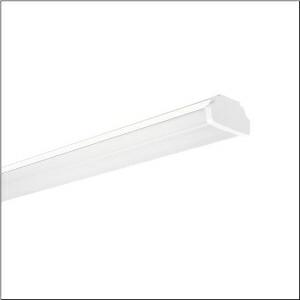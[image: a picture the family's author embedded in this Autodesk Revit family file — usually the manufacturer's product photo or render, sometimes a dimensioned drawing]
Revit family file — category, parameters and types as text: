
# Revit family: modario_r__31_gen_2_53bm8127v68xc2_4e77
name_source: partatom
category: Lighting Fixtures
units: mm (PartAtom-declared; Revit-internal decimal feet)

## family parameters
Cut with Voids When Loaded = No
Host = Face
Light Source = No
Part Type = Normal
Room Calculation Point = No
Round Connector Dimension = Use Diameter
Shared = No

## types (1)
- Modario® 31 Gen.2 (1 x LED, 8340 lm, 47.9 W, 6500K)
    Apparent Load = 48 VA
    CIE Flux Codes = 47 80 95 93 100
    Color Rendering = 80
    Color Temperature = 6500K
    Default Elevation = 1800 mm
    Description = Modario® 31 Gen.2, luminaire insert, of sheet steel, coil coated, white, length: 1.495mm, width: 81mm, height: 82mm, 5x system unit, system units: 299mm, LED rated luminous flux: 8.340lm, light colour: 865, control gear: ON/OFF, control gear: ECG, with plug, 3-pole, with phase selection, mains connection: 220..240V, AC, 50/60Hz, rated input power: 48W, through-wiring accessed according to module size, primary optical cover: cover, of PMMA, light emission: direct distribution, primary light characteristic: symmetric, protection rating (complete): IP20, protection rating (LED compartment): IP50, insulation class (complete): insulation class I (protective earthing), certification: CE, ENEC, VDE, UKCA, impact resistance: IK03, permissible ambient temperature for indoor applications: -35..+45°C, corresponds to IFS (International Featured Standards) requirements for safety and quality in the food industry, reducing of maximum allowable ambient temperature of 5°C with ceiling mounting, IP40 when using the optional accessory 5TP9018, packaging unit: 1 piece
    Height = 92 mm
    Lamp = 1 x LED
    Lamp Light Flux = 8340 lm
    Lamp Power = 47.9 W
    Lamp count = 1
    Length = 1495 mm
    Luminous efficacy = 174 lm/W
    Manufacturer = Siteco
    ModVariant = No
    Model = 53BM8127V68XC2
    Mounting Place = Ceiling
    Mounting Type = Pendant
    Number of Poles = 1
    OnlyDefault = Yes
    Power Factor = 1
    Product Name = Modario® 31 Gen.2
    Product group = luminaire insert
    ProductGroupID = 902
    Protection Class = Protection class I
    Protection Degree = IP 20
    RLX_Detail_Level = 1
    RLX_Emergency_Light_Flux = 0 lm
    RLX_Emergency_Type = 0
    RLX_Emergency_Type_DB = No
    RlxData = <blob elided: 38637 chars, md5=1f33d779>
    Socket = socket
    Standby Power = 0 W
    System Light Flux = 8340 lm
    System Power = 48 W
    Type Comments = Product without accessories
    Type Image = l_1341886.jpg
    URL = http://relux.com
    VarID = ---
    Voltage = 0 V
    Weight = 0.00 kg
    Width = 81 mm

## geometry (parser evidence)
native form markers: Blend x4, Sweep x11
no freeform markers — native parametric forms only
